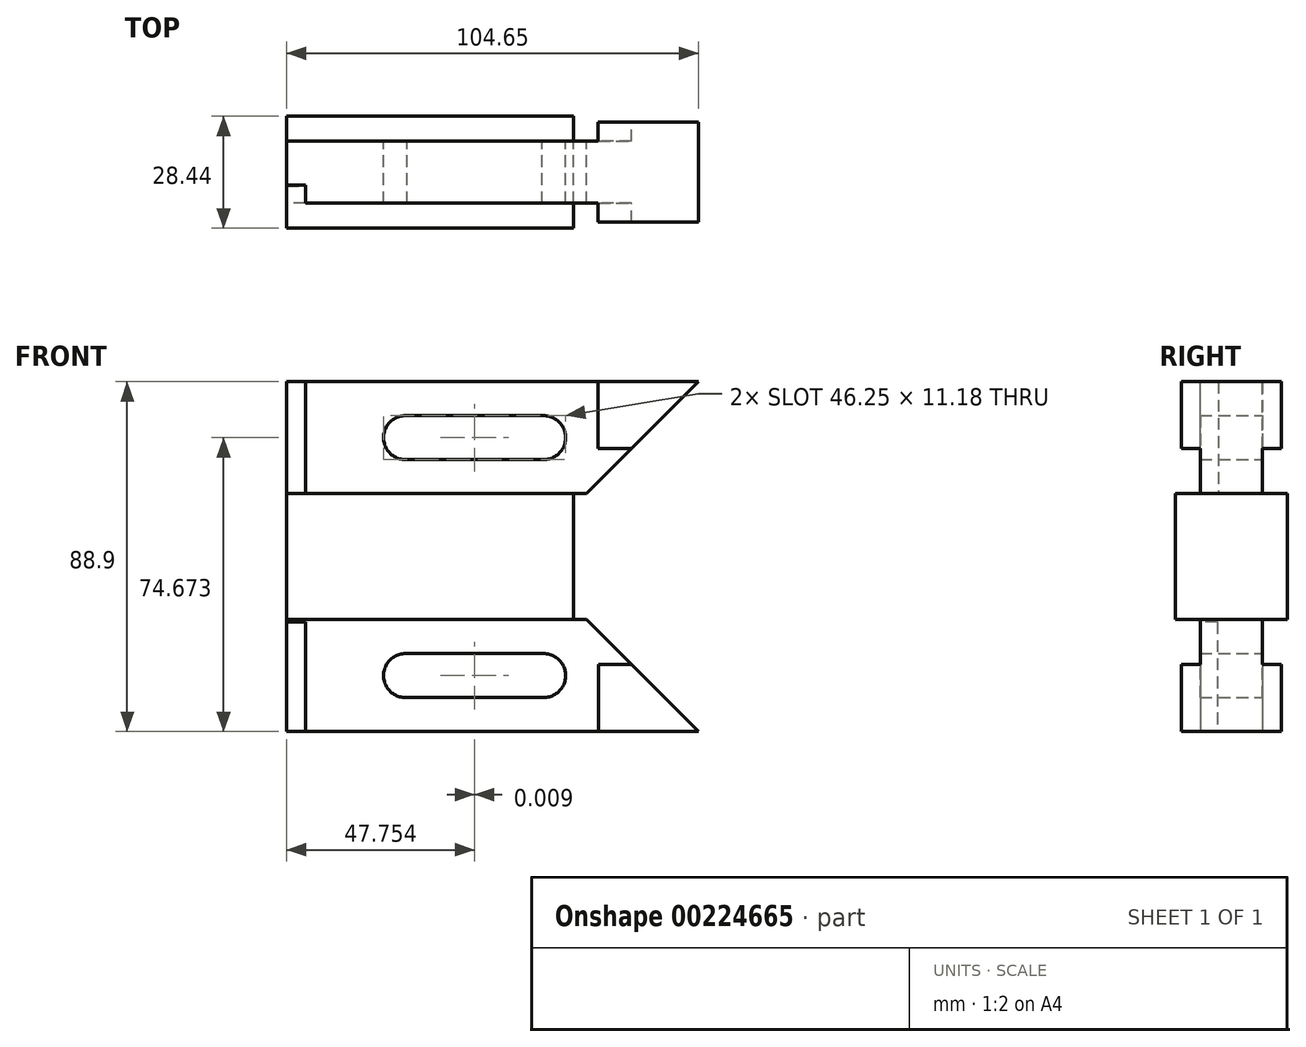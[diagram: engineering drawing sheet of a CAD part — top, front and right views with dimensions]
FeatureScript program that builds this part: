
annotation { "Feature Type Name" : "Feature", "Feature Type Description" : "" }
export const myFeature = defineFeature(function(context is Context, id is Id, definition is map)
    precondition{}
    {
        {
            var Q0;
            Q0=qCreatedBy(makeId("Front.planeOp"),FACE);
            var sketch = newSketch(context, id + "F0", { "sketchPlane" : qUnion([Q0])});
            skLineSegment(sketch, "E0.bottom", {"start": v(-48.13, 46.69) * mm, "end": v(56.52, 46.69) * mm});
            skLineSegment(sketch, "E0.top", {"start": v(-48.13, 18.24) * mm, "end": v(28.07, 18.24) * mm});
            skLineSegment(sketch, "E0.left", {"start": v(-48.13, 46.69) * mm, "end": v(-48.13, 18.24) * mm});
            skLineSegment(sketch, "E1.bottom", {"start": v(-48.13, -13.77) * mm, "end": v(28.07, -13.77) * mm});
            skLineSegment(sketch, "E1.top", {"start": v(-48.13, -42.21) * mm, "end": v(56.52, -42.21) * mm});
            skLineSegment(sketch, "E1.left", {"start": v(-48.13, -13.77) * mm, "end": v(-48.13, -42.21) * mm});
            skLineSegment(sketch, "E2.bottom", {"start": v(17.53, 26.87) * mm, "end": v(-17.53, 26.87) * mm});
            skLineSegment(sketch, "E2.top", {"start": v(17.53, 38.05) * mm, "end": v(-17.53, 38.05) * mm});
            skPoint(sketch, "E2.middle", {"position": v(0, 32.46) * mm});
            skLineSegment(sketch, "E3.bottom", {"start": v(-17.53, -22.4) * mm, "end": v(17.53, -22.4) * mm});
            skLineSegment(sketch, "E3.top", {"start": v(-17.53, -33.58) * mm, "end": v(17.53, -33.58) * mm});
            skPoint(sketch, "E3.middle", {"position": v(0, -27.99) * mm});
            skPoint(sketch, "E4.third.point", {"position": v(11.56, -27.99) * mm});
            skPoint(sketch, "E4.third.point.positionSnap0", {"position": v(17.53, -27.99) * mm});
            skPoint(sketch, "E5.third.point", {"position": v(-23.5, -27.99) * mm});
            skPoint(sketch, "E5.third.point.positionSnap0", {"position": v(-17.53, -27.99) * mm});
            skPoint(sketch, "E6.third.point", {"position": v(-20.27, 35.35) * mm});
            skPoint(sketch, "E7.third.point", {"position": v(20.56, 34.81) * mm});
            skPoint(sketch, "E8", {"position": v(22.58, 46.69) * mm});
            skPoint(sketch, "E9", {"position": v(21.46, -42.21) * mm});
            skPoint(sketch, "E10.third.point", {"position": v(11.56, -34.34) * mm});
            skPoint(sketch, "E11.third.point", {"position": v(-12.08, -27.99) * mm});
            skPoint(sketch, "E12.third.point", {"position": v(-23.5, 32.14) * mm});
            skPoint(sketch, "E13.third.point", {"position": v(11.56, 32.14) * mm});
            skPoint(sketch, "E14.middle", {"position": v(56.52, -42.21) * mm});
            skPoint(sketch, "E14.right.start.orphan", {"position": v(95.34, -28.35) * mm});
            skPoint(sketch, "E14.top.end.orphan", {"position": v(81.92, -59.1) * mm});
            skPoint(sketch, "E15.orphan", {"position": v(17.69, -56.08) * mm});
            skPoint(sketch, "E16.middle", {"position": v(56.52, 46.69) * mm});
            skPoint(sketch, "E17.orphan", {"position": v(81.79, 29.67) * mm});
            skPoint(sketch, "E16.bottom.start.orphan", {"position": v(82.04, 63.7) * mm});
            skPoint(sketch, "E18.orphan", {"position": v(31.24, 63.7) * mm});
            skLineSegment(sketch, "E19", {"start": v(-41.78, 46.69) * mm, "end": v(-41.78, 18.24) * mm});
            skLineSegment(sketch, "E20", {"start": v(-41.78, -13.77) * mm, "end": v(-41.78, -42.21) * mm});
            skPoint(sketch, "E14.bottom.start.orphan", {"position": v(31.12, -25.33) * mm});
            skLineSegment(sketch, "E21", {"start": v(31.12, -25.2) * mm, "end": v(31.12, -42.21) * mm});
            skLineSegment(sketch, "E22", {"start": v(31.12, -25.2) * mm, "end": v(39.5, -25.2) * mm});
            skLineSegment(sketch, "E23", {"start": v(56.52, 46.69) * mm, "end": v(28.07, 18.24) * mm});
            skPoint(sketch, "E24.orphan", {"position": v(56.52, 18.24) * mm});
            skLineSegment(sketch, "E25", {"start": v(56.52, -42.21) * mm, "end": v(28.07, -13.77) * mm});
            skPoint(sketch, "E16.right.end.orphan", {"position": v(30.99, 29.67) * mm});
            skPoint(sketch, "E16.right.start.orphan", {"position": v(21.46, 46.69) * mm});
            skArc(sketch, "E26", {"start": v(-17.53, 38.05) * mm, "mid": v(-23.5, 32.46) * mm, "end": v(-17.53, 26.87) * mm});
            skArc(sketch, "E27", {"start": v(16.77, 38.05) * mm, "mid": v(22.75, 32.46) * mm, "end": v(16.77, 26.87) * mm});
            skArc(sketch, "E28", {"start": v(-17.53, -22.4) * mm, "mid": v(-23.5, -27.99) * mm, "end": v(-17.53, -33.58) * mm});
            skArc(sketch, "E29", {"start": v(17.53, -33.58) * mm, "mid": v(17.16, -33.59) * mm, "end": v(16.78, -33.58) * mm});
            skLineSegment(sketch, "E30", {"start": v(30.99, 29.67) * mm, "end": v(30.99, 46.69) * mm});
            skLineSegment(sketch, "E31", {"start": v(30.99, 29.67) * mm, "end": v(39.5, 29.67) * mm});
            skLineSegment(sketch, "E32", {"start": v(-48.13, 18.24) * mm, "end": v(-48.13, -13.77) * mm});
            skArc(sketch, "E33.trimOffspring", {"start": v(16.78, -22.4) * mm, "mid": v(17.16, -22.39) * mm, "end": v(17.53, -22.4) * mm});
            skArc(sketch, "E34", {"start": v(16.78, -33.58) * mm, "mid": v(22.76, -27.99) * mm, "end": v(16.78, -22.4) * mm});
            skLineSegment(sketch, "E35", {"start": v(24.78, 18.24) * mm, "end": v(24.78, -13.77) * mm});
            skSolve(sketch);
        }
        {
            var Q0;
            {var subQ3=sQuery(id+"F0.wireOp",EDGE,"E32");Q0=makeQuery(id+"F0.imprint","IMPRINT",FACE,{"disambiguationData":[TD([[makeQuery(id+"F0.imprint","IMPRINT",EDGE,{"derivedFrom":subQ3}),1.0]])]});}
            extrude(context, id + "F1", {"entities" : qUnion([Q0]), "endBound" : BoundingType.SYMMETRIC, "depth" : 28.45 * mm});
        }
        {
            var Q0;
            {var subQ5=sQuery(id+"F0.wireOp",EDGE,"E20");Q0=makeQuery(id+"F0.imprint","IMPRINT",FACE,{"disambiguationData":[TD([[makeQuery(id+"F0.imprint","IMPRINT",EDGE,{"derivedFrom":subQ5}),1.0]])]});}
            var Q1;
            {var subQ5=sQuery(id+"F0.wireOp",EDGE,"E19");Q1=makeQuery(id+"F0.imprint","IMPRINT",FACE,{"disambiguationData":[TD([[makeQuery(id+"F0.imprint","IMPRINT",EDGE,{"derivedFrom":subQ5}),1.0]])]});}
            var Q2;
            {var subQ0=sQuery(id+"F0.wireOp",EDGE,"E0.left");Q2=makeQuery(id+"F0.imprint","IMPRINT",FACE,{"disambiguationData":[TD([[makeQuery(id+"F0.imprint","IMPRINT",EDGE,{"derivedFrom":subQ0}),1.0]])]});}
            var Q3;
            {var subQ0=sQuery(id+"F0.wireOp",EDGE,"E1.left");Q3=makeQuery(id+"F0.imprint","IMPRINT",FACE,{"disambiguationData":[TD([[makeQuery(id+"F0.imprint","IMPRINT",EDGE,{"derivedFrom":subQ0}),1.0]])]});}
            extrude(context, id + "F2", {"entities" : qUnion([Q0, Q1, Q2, Q3]), "operationType" : NewBodyOperationType.ADD, "endBound" : BoundingType.SYMMETRIC, "depth" : 15.75 * mm});
        }
        {
            var Q0;
            {var subQ5=sQuery(id+"F0.wireOp",EDGE,"E19");Q0=makeQuery(id+"F0.imprint","IMPRINT",FACE,{"disambiguationData":[TD([[makeQuery(id+"F0.imprint","IMPRINT",EDGE,{"derivedFrom":subQ5}),1.0]])]});}
            var Q1;
            {var subQ0=sQuery(id+"F0.wireOp",EDGE,"E0.left");Q1=makeQuery(id+"F0.imprint","IMPRINT",FACE,{"disambiguationData":[TD([[makeQuery(id+"F0.imprint","IMPRINT",EDGE,{"derivedFrom":subQ0}),1.0]])]});}
            var Q2;
            {var subQ0=sQuery(id+"F0.wireOp",EDGE,"E1.left");Q2=makeQuery(id+"F0.imprint","IMPRINT",FACE,{"disambiguationData":[TD([[makeQuery(id+"F0.imprint","IMPRINT",EDGE,{"derivedFrom":subQ0}),1.0]])]});}
            var Q3;
            {var subQ5=sQuery(id+"F0.wireOp",EDGE,"E20");Q3=makeQuery(id+"F0.imprint","IMPRINT",FACE,{"disambiguationData":[TD([[makeQuery(id+"F0.imprint","IMPRINT",EDGE,{"derivedFrom":subQ5}),1.0]])]});}
            extrude(context, id + "F3", {"entities" : qUnion([Q0, Q1, Q2, Q3]), "operationType" : NewBodyOperationType.ADD, "endBound" : BoundingType.SYMMETRIC, "depth" : 15.75 * mm});
        }
        {
            var Q0;
            {var subQ3=sQuery(id+"F0.wireOp",EDGE,"E30");Q0=makeQuery(id+"F0.imprint","IMPRINT",FACE,{"disambiguationData":[TD([[makeQuery(id+"F0.imprint","IMPRINT",EDGE,{"derivedFrom":subQ3}),-1.0]])]});}
            var Q1;
            {var subQ3=sQuery(id+"F0.wireOp",EDGE,"E21");Q1=makeQuery(id+"F0.imprint","IMPRINT",FACE,{"disambiguationData":[TD([[makeQuery(id+"F0.imprint","IMPRINT",EDGE,{"derivedFrom":subQ3}),1.0]])]});}
            extrude(context, id + "F4", {"entities" : qUnion([Q0, Q1]), "operationType" : NewBodyOperationType.ADD, "endBound" : BoundingType.SYMMETRIC, "depth" : 25.4 * mm});
        }
        {
            var Q0;
            Q0=makeQuery(id+"F2.opExtrude","CAP_FACE",FACE,{"disambiguationData":[OSD([sQuery(id+"F0.wireOp",EDGE,"E0.bottom"),sQuery(id+"F0.wireOp",EDGE,"E0.top"),sQuery(id+"F0.wireOp",EDGE,"E0.left"),sQuery(id+"F0.wireOp",EDGE,"E2.bottom"),sQuery(id+"F0.wireOp",EDGE,"E2.top"),sQuery(id+"F0.wireOp",EDGE,"E23"),sQuery(id+"F0.wireOp",EDGE,"E26"),sQuery(id+"F0.wireOp",EDGE,"E27"),sQuery(id+"F0.wireOp",EDGE,"E30"),sQuery(id+"F0.wireOp",EDGE,"E31")])],"isStart":false});
            var sketch = newSketch(context, id + "F5", { "sketchPlane" : qUnion([Q0])});
            skLineSegment(sketch, "E36.bottom", {"start": v(-43.36, 18.24) * mm, "end": v(-48.13, 18.24) * mm});
            skLineSegment(sketch, "E36.top", {"start": v(-43.36, 54.05) * mm, "end": v(-48.13, 54.05) * mm});
            skLineSegment(sketch, "E36.left", {"start": v(-43.36, 18.24) * mm, "end": v(-43.36, 54.05) * mm});
            skLineSegment(sketch, "E36.right", {"start": v(-48.13, 18.24) * mm, "end": v(-48.13, 54.05) * mm});
            skLineSegment(sketch, "E37.bottom", {"start": v(-43.36, -14.4) * mm, "end": v(-51.06, -14.4) * mm});
            skLineSegment(sketch, "E37.top", {"start": v(-43.36, -45.21) * mm, "end": v(-51.06, -45.21) * mm});
            skLineSegment(sketch, "E37.left", {"start": v(-43.36, -14.4) * mm, "end": v(-43.36, -45.21) * mm});
            skLineSegment(sketch, "E37.right", {"start": v(-51.06, -14.4) * mm, "end": v(-51.06, -45.21) * mm});
            skSolve(sketch);
        }
        {
            var Q0;
            {var subQ0=sQuery(id+"F5.wireOp",EDGE,"E36.bottom");Q0=makeQuery(id+"F5.imprint","IMPRINT",FACE,{"disambiguationData":[TD([[makeQuery(id+"F5.imprint","IMPRINT",EDGE,{"derivedFrom":subQ0}),1.0]])]});}
            extrude(context, id + "F6", {"entities" : qUnion([Q0]), "operationType" : NewBodyOperationType.REMOVE, "endBound" : BoundingType.SYMMETRIC, "oppositeDirection" : true, "depth" : 9.14 * mm});
        }
        {
            var Q0;
            Q0=makeQuery(id+"F5.imprint","IMPRINT",FACE,{"disambiguationData":[TD([[makeQuery(id+"F5.imprint","IMPRINT",EDGE,{"derivedFrom":sQuery(id+"F5.wireOp",EDGE,"E37.bottom")}),1.0]])]});
            var Q1;
            {var subQ0=sQuery(id+"F5.wireOp",EDGE,"E36.bottom");Q1=makeQuery(id+"F5.imprint","IMPRINT",FACE,{"disambiguationData":[TD([[makeQuery(id+"F5.imprint","IMPRINT",EDGE,{"derivedFrom":subQ0}),1.0]])]});}
            extrude(context, id + "F7", {"entities" : qUnion([Q0, Q1]), "operationType" : NewBodyOperationType.REMOVE, "endBound" : BoundingType.SYMMETRIC, "oppositeDirection" : true, "depth" : 8.64 * mm});
        }
    });
